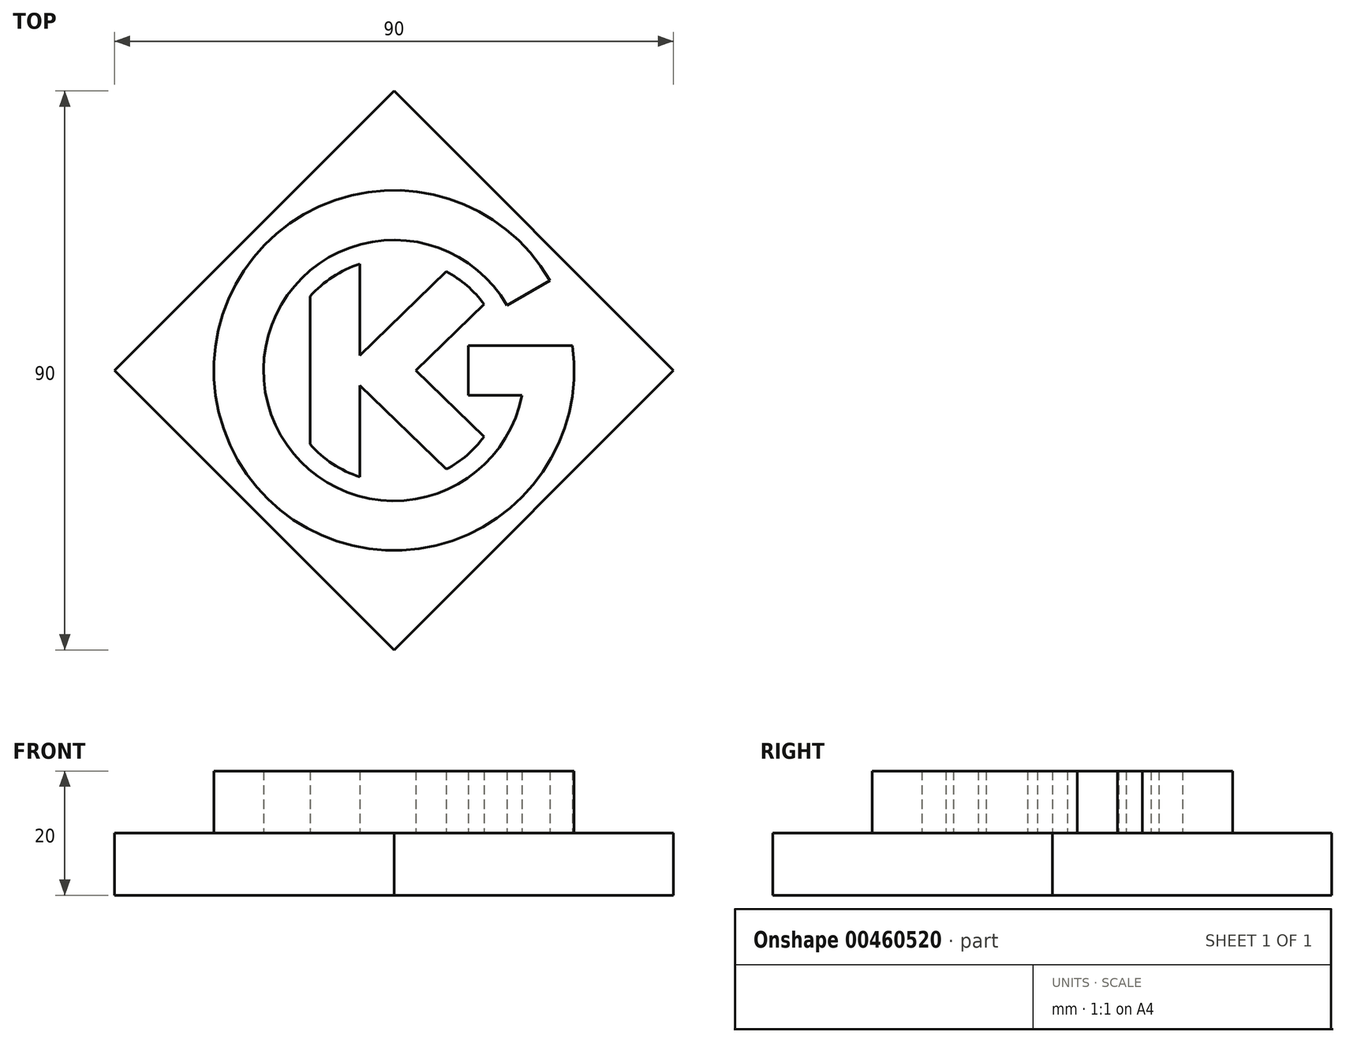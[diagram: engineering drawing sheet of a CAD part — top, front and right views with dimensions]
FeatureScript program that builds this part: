
annotation { "Feature Type Name" : "Feature", "Feature Type Description" : "" }
export const myFeature = defineFeature(function(context is Context, id is Id, definition is map)
    precondition{}
    {
        {
            var Q0;
            Q0=qCreatedBy(makeId("Top.planeOp"),FACE);
            var sketch = newSketch(context, id + "F0", { "sketchPlane" : qUnion([Q0])});
            skLineSegment(sketch, "E0", {"start": v(0, 45) * mm, "end": v(-45, 0) * mm});
            skLineSegment(sketch, "E1", {"start": v(-45, 0) * mm, "end": v(0, -45) * mm});
            skLineSegment(sketch, "E2", {"start": v(0, -45) * mm, "end": v(45, 0) * mm});
            skLineSegment(sketch, "E3", {"start": v(45, 0) * mm, "end": v(0, 45) * mm});
            skSolve(sketch);
        }
        {
            var Q0;
            Q0 = qSketchRegion(id + "F0", true);
            extrude(context, id + "F1", {"entities" : qUnion([Q0]), "depth" : 10 * mm});
        }
        {
            var Q0;
            Q0=makeQuery(id+"F1.opExtrude","CAP_FACE",FACE,{"disambiguationData":[OSD([sQuery(id+"F0.wireOp",EDGE,"E0"),sQuery(id+"F0.wireOp",EDGE,"E1"),sQuery(id+"F0.wireOp",EDGE,"E2"),sQuery(id+"F0.wireOp",EDGE,"E3")])],"isStart":false});
            var sketch = newSketch(context, id + "F2", { "sketchPlane" : qUnion([Q0])});
            skArc(sketch, "E4", {"start": v(25.11, 14.5) * mm, "mid": v(-27.43, -9.42) * mm, "end": v(28.72, 4) * mm});
            skArc(sketch, "E5", {"start": v(18.19, 10.5) * mm, "mid": v(-20.71, -3.47) * mm, "end": v(20.62, -4) * mm});
            skLineSegment(sketch, "E6", {"start": v(18.19, 10.5) * mm, "end": v(25.11, 14.5) * mm});
            skLineSegment(sketch, "E7", {"start": v(11.6, 4) * mm, "end": v(28.72, 4) * mm});
            skLineSegment(sketch, "E8", {"start": v(11.98, -4) * mm, "end": v(20.62, -4) * mm});
            skLineSegment(sketch, "E9", {"start": v(12, 4) * mm, "end": v(12, -4) * mm});
            skSolve(sketch);
        }
        {
            var Q0;
            Q0 = qSketchRegion(id + "F2", true);
            extrude(context, id + "F3", {"entities" : qUnion([Q0]), "operationType" : NewBodyOperationType.ADD, "depth" : 10 * mm});
        }
        {
            var Q0;
            Q0=makeQuery(id+"F1.opExtrude","CAP_FACE",FACE,{"disambiguationData":[OSD([sQuery(id+"F0.wireOp",EDGE,"E0"),sQuery(id+"F0.wireOp",EDGE,"E1"),sQuery(id+"F0.wireOp",EDGE,"E2"),sQuery(id+"F0.wireOp",EDGE,"E3")])],"isStart":false});
            var sketch = newSketch(context, id + "F4", { "sketchPlane" : qUnion([Q0])});
            skArc(sketch, "E10", {"start": v(14.5, 10.67) * mm, "mid": v(11.75, 13.63) * mm, "end": v(8.42, 15.91) * mm});
            skLineSegment(sketch, "E11", {"start": v(-5.5, 17.14) * mm, "end": v(-5.5, -17.14) * mm});
            skLineSegment(sketch, "E12", {"start": v(-13.5, 11.9) * mm, "end": v(-13.5, -11.9) * mm});
            skLineSegment(sketch, "E13", {"start": v(14.5, 10.67) * mm, "end": v(3.5, 0) * mm});
            skLineSegment(sketch, "E14", {"start": v(14.5, -10.67) * mm, "end": v(3.5, 0) * mm});
            skLineSegment(sketch, "E15", {"start": v(8.42, -15.91) * mm, "end": v(-5.5, -2.42) * mm});
            skArc(sketch, "E16.trimOffspring", {"start": v(8.42, -15.91) * mm, "mid": v(11.75, -13.63) * mm, "end": v(14.5, -10.67) * mm});
            skArc(sketch, "E17.trimOffspring", {"start": v(-13.5, -11.9) * mm, "mid": v(-9.85, -15.06) * mm, "end": v(-5.5, -17.14) * mm});
            skLineSegment(sketch, "E18.trimOffspring", {"start": v(8.42, 15.91) * mm, "end": v(-5.5, 2.42) * mm});
            skArc(sketch, "E19.trimOffspring", {"start": v(-5.5, 17.14) * mm, "mid": v(-9.85, 15.06) * mm, "end": v(-13.5, 11.9) * mm});
            skSolve(sketch);
        }
        {
            var Q0;
            Q0 = qSketchRegion(id + "F4", true);
            extrude(context, id + "F5", {"entities" : qUnion([Q0]), "operationType" : NewBodyOperationType.ADD, "depth" : 10 * mm});
        }
    });
